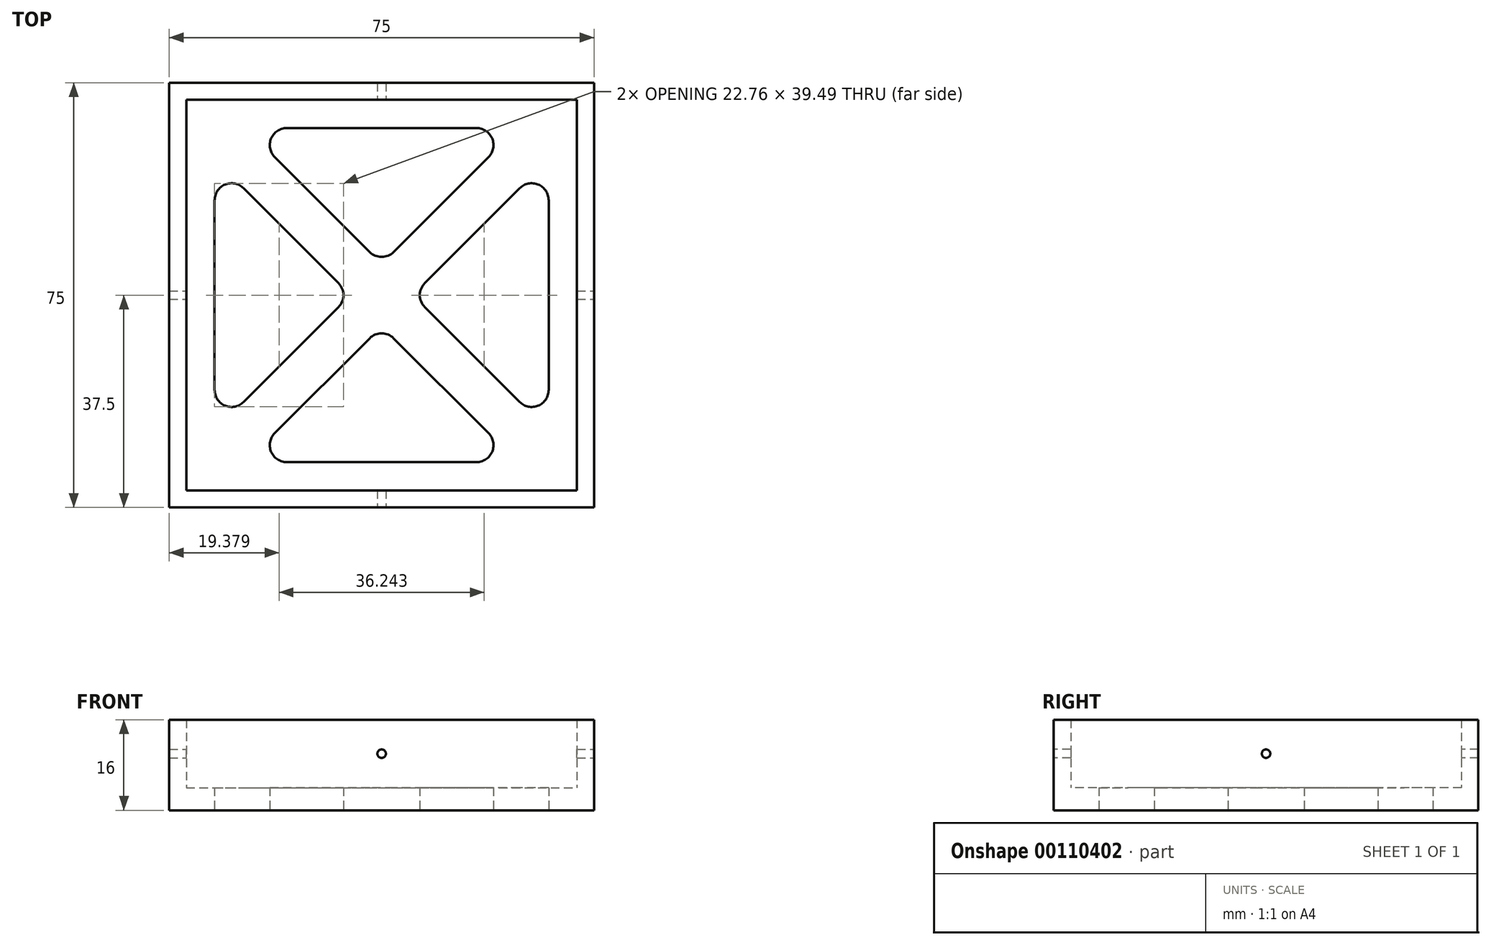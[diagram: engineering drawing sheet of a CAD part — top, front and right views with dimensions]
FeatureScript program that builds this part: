
annotation { "Feature Type Name" : "Feature", "Feature Type Description" : "" }
export const myFeature = defineFeature(function(context is Context, id is Id, definition is map)
    precondition{}
    {
        {
            var Q0;
            Q0=qCreatedBy(makeId("Top.planeOp"),FACE);
            var sketch = newSketch(context, id + "F0", { "sketchPlane" : qUnion([Q0])});
            skLineSegment(sketch, "E0.bottom", {"start": v(0, 0) * mm, "end": v(75, 0) * mm});
            skLineSegment(sketch, "E0.top", {"start": v(0, 75) * mm, "end": v(75, 75) * mm});
            skLineSegment(sketch, "E0.left", {"start": v(0, 0) * mm, "end": v(0, 75) * mm});
            skLineSegment(sketch, "E0.right", {"start": v(75, 0) * mm, "end": v(75, 75) * mm});
            skSolve(sketch);
        }
        {
            var Q0;
            Q0 = qSketchRegion(id + "F0", true);
            extrude(context, id + "F1", {"entities" : qUnion([Q0]), "depth" : 4 * mm});
        }
        {
            var Q0;
            Q0=makeQuery(id+"F1.opExtrude","CAP_FACE",FACE,{"disambiguationData":[OSD([sQuery(id+"F0.wireOp",EDGE,"E0.bottom"),sQuery(id+"F0.wireOp",EDGE,"E0.top"),sQuery(id+"F0.wireOp",EDGE,"E0.left"),sQuery(id+"F0.wireOp",EDGE,"E0.right")])],"isStart":false});
            var sketch = newSketch(context, id + "F2", { "sketchPlane" : qUnion([Q0])});
            skLineSegment(sketch, "E1.bottom", {"start": v(0, 75) * mm, "end": v(75, 75) * mm});
            skLineSegment(sketch, "E1.top", {"start": v(0, 0) * mm, "end": v(75, 0) * mm});
            skLineSegment(sketch, "E1.left", {"start": v(0, 75) * mm, "end": v(0, 0) * mm});
            skLineSegment(sketch, "E1.right", {"start": v(75, 75) * mm, "end": v(75, 0) * mm});
            skLineSegment(sketch, "E2.bottom", {"start": v(3, 72) * mm, "end": v(72, 72) * mm});
            skLineSegment(sketch, "E2.top", {"start": v(3, 3) * mm, "end": v(72, 3) * mm});
            skLineSegment(sketch, "E2.left", {"start": v(3, 72) * mm, "end": v(3, 3) * mm});
            skLineSegment(sketch, "E2.right", {"start": v(72, 72) * mm, "end": v(72, 3) * mm});
            skSolve(sketch);
        }
        {
            var Q0;
            Q0 = qSketchRegion(id + "F2", true);
            extrude(context, id + "F3", {"entities" : qUnion([Q0]), "operationType" : NewBodyOperationType.ADD, "depth" : 12 * mm});
        }
        {
            var Q0;
            Q0=makeQuery(id+"F1.opExtrude","CAP_FACE",FACE,{"disambiguationData":[OSD([sQuery(id+"F0.wireOp",EDGE,"E0.bottom"),sQuery(id+"F0.wireOp",EDGE,"E0.top"),sQuery(id+"F0.wireOp",EDGE,"E0.left"),sQuery(id+"F0.wireOp",EDGE,"E0.right")])],"isStart":true});
            var sketch = newSketch(context, id + "F4", { "sketchPlane" : qUnion([Q0])});
            skLineSegment(sketch, "E3", {"start": v(8, -20.74) * mm, "end": v(8, -54.26) * mm});
            skLineSegment(sketch, "E4", {"start": v(13.12, -56.38) * mm, "end": v(29.88, -39.62) * mm});
            skPoint(sketch, "E4.endSnap0", {"position": v(0, -37.5) * mm});
            skLineSegment(sketch, "E5", {"start": v(29.88, -35.38) * mm, "end": v(13.12, -18.62) * mm});
            skLineSegment(sketch, "E6", {"start": v(37.5, 0) * mm, "end": v(37.5, -37.5) * mm, "construction": true});
            skPoint(sketch, "E7.center", {"position": v(37.5, -37.5) * mm});
            skLineSegment(sketch, "E8.1.3.0", {"start": v(39.62, -29.88) * mm, "end": v(56.38, -13.12) * mm});
            skLineSegment(sketch, "E8.3.3.0", {"start": v(54.26, -8) * mm, "end": v(20.74, -8) * mm});
            skLineSegment(sketch, "E8.6.3.0", {"start": v(18.62, -13.12) * mm, "end": v(35.38, -29.88) * mm});
            skLineSegment(sketch, "E9", {"start": v(0, -75) * mm, "end": v(75, 0) * mm, "construction": true});
            skLineSegment(sketch, "E10.MirrorCS", {"start": v(67, -20.74) * mm, "end": v(67, -54.26) * mm});
            skLineSegment(sketch, "E11.MirrorCS", {"start": v(61.88, -56.38) * mm, "end": v(45.12, -39.62) * mm});
            skLineSegment(sketch, "E12.MirrorCS", {"start": v(45.12, -35.38) * mm, "end": v(61.88, -18.62) * mm});
            skLineSegment(sketch, "E13.MirrorCS", {"start": v(39.62, -45.12) * mm, "end": v(56.38, -61.88) * mm});
            skLineSegment(sketch, "E14.MirrorCS", {"start": v(54.26, -67) * mm, "end": v(20.74, -67) * mm});
            skLineSegment(sketch, "E15.MirrorCS", {"start": v(18.62, -61.88) * mm, "end": v(35.38, -45.12) * mm});
            skPoint(sketch, "E16.visualSharp", {"position": v(13.5, -8) * mm});
            skArc(sketch, "E16.filletArc", {"start": v(20.74, -8) * mm, "mid": v(17.97, -9.85) * mm, "end": v(18.62, -13.12) * mm});
            skPoint(sketch, "E17.visualSharp", {"position": v(61.5, -8) * mm});
            skArc(sketch, "E17.filletArc", {"start": v(56.38, -13.12) * mm, "mid": v(57.03, -9.85) * mm, "end": v(54.26, -8) * mm});
            skPoint(sketch, "E18.visualSharp", {"position": v(67, -13.5) * mm});
            skArc(sketch, "E18.filletArc", {"start": v(67, -20.74) * mm, "mid": v(65.15, -17.97) * mm, "end": v(61.88, -18.62) * mm});
            skPoint(sketch, "E19.visualSharp", {"position": v(67, -61.5) * mm});
            skArc(sketch, "E19.filletArc", {"start": v(61.88, -56.38) * mm, "mid": v(65.15, -57.03) * mm, "end": v(67, -54.26) * mm});
            skPoint(sketch, "E20.visualSharp", {"position": v(43, -37.5) * mm});
            skArc(sketch, "E20.filletArc", {"start": v(45.12, -35.38) * mm, "mid": v(44.24, -37.5) * mm, "end": v(45.12, -39.62) * mm});
            skPoint(sketch, "E21.visualSharp", {"position": v(37.5, -32) * mm});
            skArc(sketch, "E21.filletArc", {"start": v(35.38, -29.88) * mm, "mid": v(37.5, -30.76) * mm, "end": v(39.62, -29.88) * mm});
            skPoint(sketch, "E22.visualSharp", {"position": v(32, -37.5) * mm});
            skArc(sketch, "E22.filletArc", {"start": v(29.88, -39.62) * mm, "mid": v(30.76, -37.5) * mm, "end": v(29.88, -35.38) * mm});
            skPoint(sketch, "E23.visualSharp", {"position": v(37.5, -43) * mm});
            skArc(sketch, "E23.filletArc", {"start": v(39.62, -45.12) * mm, "mid": v(37.5, -44.24) * mm, "end": v(35.38, -45.12) * mm});
            skPoint(sketch, "E24.visualSharp", {"position": v(8, -13.5) * mm});
            skArc(sketch, "E24.filletArc", {"start": v(13.12, -18.62) * mm, "mid": v(9.85, -17.97) * mm, "end": v(8, -20.74) * mm});
            skPoint(sketch, "E25.visualSharp", {"position": v(8, -61.5) * mm});
            skArc(sketch, "E25.filletArc", {"start": v(8, -54.26) * mm, "mid": v(9.85, -57.03) * mm, "end": v(13.12, -56.38) * mm});
            skPoint(sketch, "E26.visualSharp", {"position": v(13.5, -67) * mm});
            skArc(sketch, "E26.filletArc", {"start": v(18.62, -61.88) * mm, "mid": v(17.97, -65.15) * mm, "end": v(20.74, -67) * mm});
            skPoint(sketch, "E27.visualSharp", {"position": v(61.5, -67) * mm});
            skArc(sketch, "E27.filletArc", {"start": v(54.26, -67) * mm, "mid": v(57.03, -65.15) * mm, "end": v(56.38, -61.88) * mm});
            skSolve(sketch);
        }
        {
            var Q0;
            Q0 = qSketchRegion(id + "F4", true);
            extrude(context, id + "F5", {"entities" : qUnion([Q0]), "operationType" : NewBodyOperationType.REMOVE, "oppositeDirection" : true, "depth" : 25 * mm});
        }
        {
            var Q0;
            Q0=makeQuery(id+"F3.opExtrude","SWEPT_FACE",FACE,{"disambiguationData":[OSD([sQuery(id+"F2.wireOp",EDGE,"E2.bottom")])]});
            var sketch = newSketch(context, id + "F6", { "sketchPlane" : qUnion([Q0])});
            skCircle(sketch, "E28", {"center": v(37.5, 10) * mm, "radius": 0.75 * mm});
            skPoint(sketch, "E28.centerSnap0", {"position": v(3, 10) * mm});
            skPoint(sketch, "E28.centerSnap1", {"position": v(37.5, 4) * mm});
            skSolve(sketch);
        }
        {
            var Q0;
            Q0 = qSketchRegion(id + "F6", true);
            extrude(context, id + "F7", {"entities" : qUnion([Q0]), "operationType" : NewBodyOperationType.REMOVE, "oppositeDirection" : true, "depth" : 25 * mm, "hasSecondDirection" : true, "secondDirectionBound" : BoundingType.THROUGH_ALL, "secondDirectionOppositeDirection" : false, "secondDirectionDepth" : 25 * mm});
        }
        {
            var Q0;
            Q0=makeQuery(id+"F3.opExtrude","SWEPT_FACE",FACE,{"disambiguationData":[OSD([sQuery(id+"F2.wireOp",EDGE,"E2.left")])]});
            var sketch = newSketch(context, id + "F8", { "sketchPlane" : qUnion([Q0])});
            skCircle(sketch, "E29", {"center": v(37.5, 10) * mm, "radius": 0.75 * mm});
            skPoint(sketch, "E29.centerSnap0", {"position": v(37.5, 4) * mm});
            skPoint(sketch, "E29.centerSnap1", {"position": v(3, 10) * mm});
            skSolve(sketch);
        }
        {
            var Q0;
            Q0 = qSketchRegion(id + "F8", true);
            extrude(context, id + "F9", {"entities" : qUnion([Q0]), "operationType" : NewBodyOperationType.REMOVE, "oppositeDirection" : true, "depth" : 25 * mm, "hasSecondDirection" : true, "secondDirectionBound" : BoundingType.THROUGH_ALL, "secondDirectionOppositeDirection" : false, "secondDirectionDepth" : 25 * mm});
        }
    });
